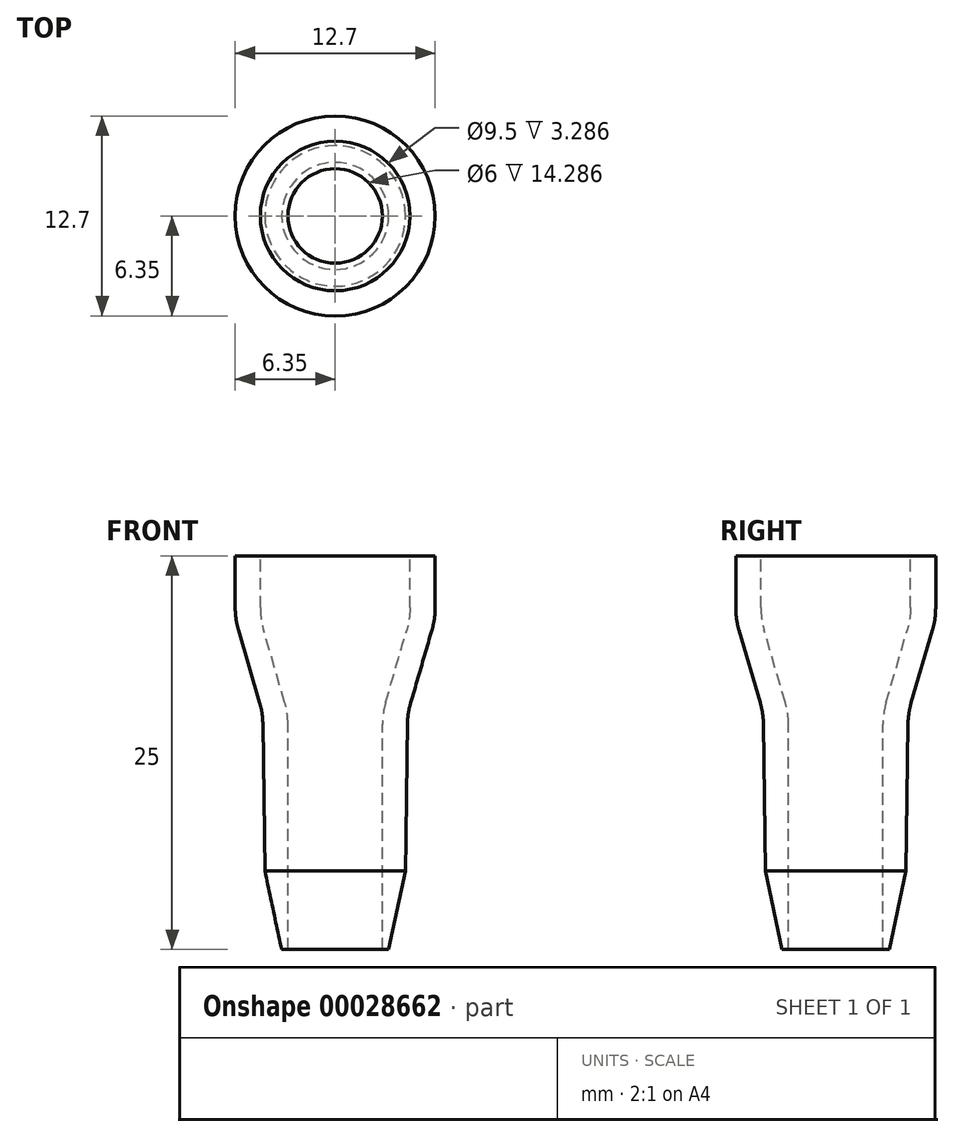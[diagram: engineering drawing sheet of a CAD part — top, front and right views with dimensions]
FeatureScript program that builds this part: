
annotation { "Feature Type Name" : "Feature", "Feature Type Description" : "" }
export const myFeature = defineFeature(function(context is Context, id is Id, definition is map)
    precondition{}
    {
        {
            var Q0;
            Q0=qCreatedBy(makeId("Front.planeOp"),FACE);
            var sketch = newSketch(context, id + "F0", { "sketchPlane" : qUnion([Q0])});
            skLineSegment(sketch, "E0", {"start": v(-4.75, 4) * mm, "end": v(-6.35, 4) * mm});
            skLineSegment(sketch, "E1", {"start": v(-6.35, 4) * mm, "end": v(-6.35, 0) * mm});
            skLineSegment(sketch, "E2", {"start": v(-6.35, 0) * mm, "end": v(-4.6, -6) * mm});
            skLineSegment(sketch, "E3", {"start": v(-4.6, -6) * mm, "end": v(-4.4, -21) * mm});
            skLineSegment(sketch, "E4", {"start": v(-4.4, -21) * mm, "end": v(-3, -21) * mm});
            skLineSegment(sketch, "E5", {"start": v(-3, -21) * mm, "end": v(-3, -6) * mm});
            skLineSegment(sketch, "E6", {"start": v(-3, -6) * mm, "end": v(-4.75, 0) * mm});
            skLineSegment(sketch, "E7", {"start": v(-4.75, 0) * mm, "end": v(-4.75, 4) * mm});
            skLineSegment(sketch, "E8", {"start": v(0, 11.85) * mm, "end": v(0, -22.33) * mm, "construction": true});
            skSolve(sketch);
        }
        {
            var Q0;
            Q0=makeQuery(id+"F0.imprint","IMPRINT",FACE,{"disambiguationData":[TD([[makeQuery(id+"F0.imprint","IMPRINT",EDGE,{"derivedFrom":sQuery(id+"F0.wireOp",EDGE,"E0")}),1.0]])]});
            var Q1;
            Q1=sQuery(id+"F0.wireOp",EDGE,"E8");
            revolve(context, id + "F1", {"surfaceOperationType" : NewSurfaceOperationType.NEW, "entities" : qUnion([Q0]), "axis" : qUnion([Q1]), "revolveType" : RevolveType.FULL});
        }
        {
            var Q0;
            Q0=makeQuery(id+"F1.opRevolve","SWEPT_EDGE",EDGE,{"disambiguationData":[OSD([sQuery(id+"F0.wireOp",EDGE,"E6"),sQuery(id+"F0.wireOp",EDGE,"E7")])]});
            var Q1;
            Q1=makeQuery(id+"F1.opRevolve","SWEPT_EDGE",EDGE,{"disambiguationData":[OSD([sQuery(id+"F0.wireOp",EDGE,"E5"),sQuery(id+"F0.wireOp",EDGE,"E6")])]});
            var Q2;
            Q2=makeQuery(id+"F1.opRevolve","SWEPT_EDGE",EDGE,{"disambiguationData":[OSD([sQuery(id+"F0.wireOp",EDGE,"E2"),sQuery(id+"F0.wireOp",EDGE,"E3")])]});
            var Q3;
            Q3=makeQuery(id+"F1.opRevolve","SWEPT_EDGE",EDGE,{"disambiguationData":[OSD([sQuery(id+"F0.wireOp",EDGE,"E1"),sQuery(id+"F0.wireOp",EDGE,"E2")])]});
            fillet(context, id + "F2", {"entities" : qUnion([Q0, Q1, Q2, Q3]), "tangentPropagation" : true, "radius" : 5 * mm, "defaultsChanged" : false, "vertexSettings" : [], "allowEdgeOverflow" : false});
        }
        {
            var Q0;
            Q0=makeQuery(id+"F1.opRevolve","SWEPT_EDGE",EDGE,{"disambiguationData":[OSD([sQuery(id+"F0.wireOp",EDGE,"E3"),sQuery(id+"F0.wireOp",EDGE,"E4")])]});
            chamfer(context, id + "F3", {"entities" : qUnion([Q0]), "chamferType" : ChamferType.TWO_OFFSETS, "width1" : 5 * mm, "oppositeDirection" : false, "width2" : 1 * mm, "tangentPropagation" : true});
        }
    });
